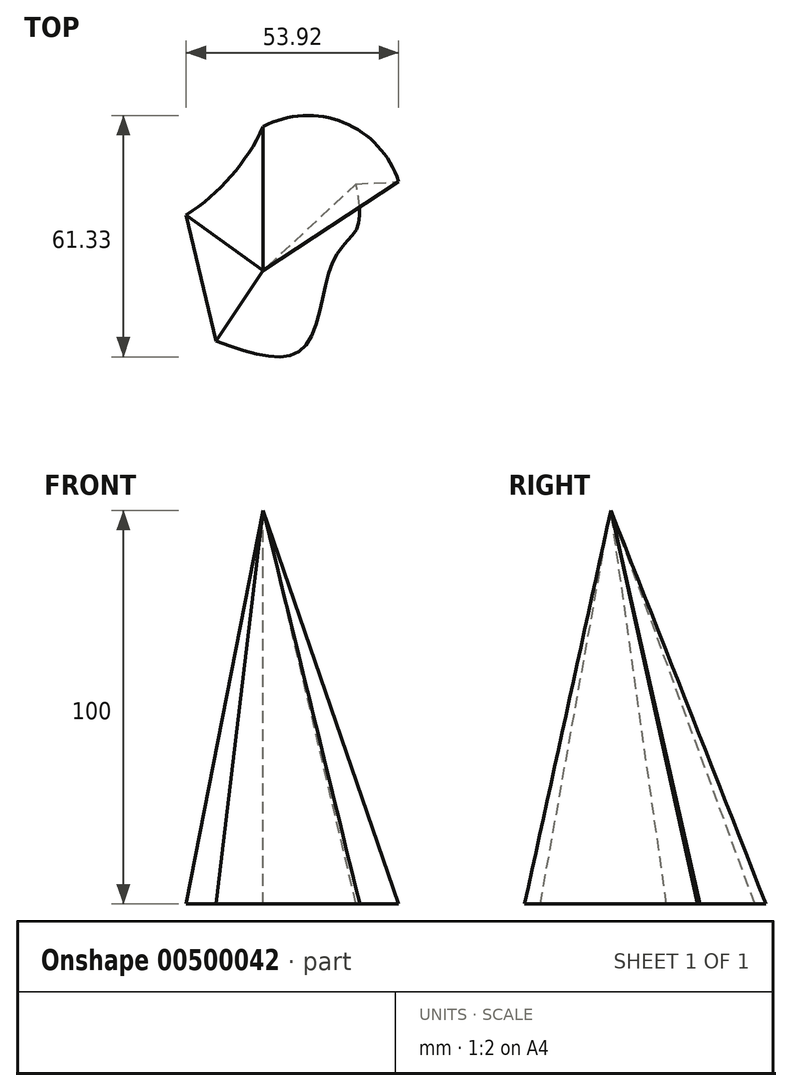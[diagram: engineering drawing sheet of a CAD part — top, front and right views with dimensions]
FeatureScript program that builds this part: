
annotation { "Feature Type Name" : "Feature", "Feature Type Description" : "" }
export const myFeature = defineFeature(function(context is Context, id is Id, definition is map)
    precondition{}
    {
        {
            var Q0;
            Q0=qCreatedBy(makeId("Top.planeOp"),FACE);
            var sketch = newSketch(context, id + "F0", { "sketchPlane" : qUnion([Q0])});
            skArc(sketch, "E0", {"start": v(34.4, 22.59) * mm, "mid": v(20.46, 37.62) * mm, "end": v(0, 36.58) * mm});
            skArc(sketch, "E1", {"start": v(-19.53, 14.14) * mm, "mid": v(-8.14, 23.95) * mm, "end": v(0, 36.58) * mm});
            skLineSegment(sketch, "E2", {"start": v(-19.53, 14.14) * mm, "end": v(-11.95, -17.93) * mm});
            skFitSpline(sketch, "E3", {"points": [v(-11.95, -17.93) * mm, v(9.91, -19.97) * mm, v(17.78, 2.48) * mm, v(23.9, 10.93) * mm, v(23.6, 22) * mm], "startDerivative": vector(89.37, -31.6) * mm, "endDerivative": vector(-10.96, 59.76) * mm});
            skLineSegment(sketch, "E4", {"start": v(23.6, 22) * mm, "end": v(34.4, 22.59) * mm});
            skSolve(sketch);
        }
        {
            var Q0;
            Q0=qCreatedBy(makeId("Top.planeOp"),FACE);
            cPlane(context, id + "F1", {"entities" : qUnion([Q0]), "cplaneType" : CPlaneType.OFFSET, "offset" : 100 * mm, "width" : 152.4 * mm, "height" : 152.4 * mm});
        }
        {
            var Q0;
            Q0=qCreatedBy(id+"F1.planeOp",FACE);
            var sketch = newSketch(context, id + "F2", { "sketchPlane" : qUnion([Q0])});
            skPoint(sketch, "E5", {"position": v(0, 0) * mm});
            skSolve(sketch);
        }
        {
            var Q0;
            Q0=makeQuery(id+"F0.imprint","IMPRINT",FACE,{"disambiguationData":[TD([[makeQuery(id+"F0.imprint","IMPRINT",EDGE,{"derivedFrom":sQuery(id+"F0.wireOp",EDGE,"E0")}),1.0]])]});
            var Q1;
            Q1=sQuery(id+"F2.wireOp",VERTEX,"E5");
            loft(context, id + "F3", {"sheetProfilesArray" : [{ "sheetProfileEntities" : qUnion([Q0]) }, { "sheetProfileEntities" : qUnion([Q1]) }]});
        }
    });
